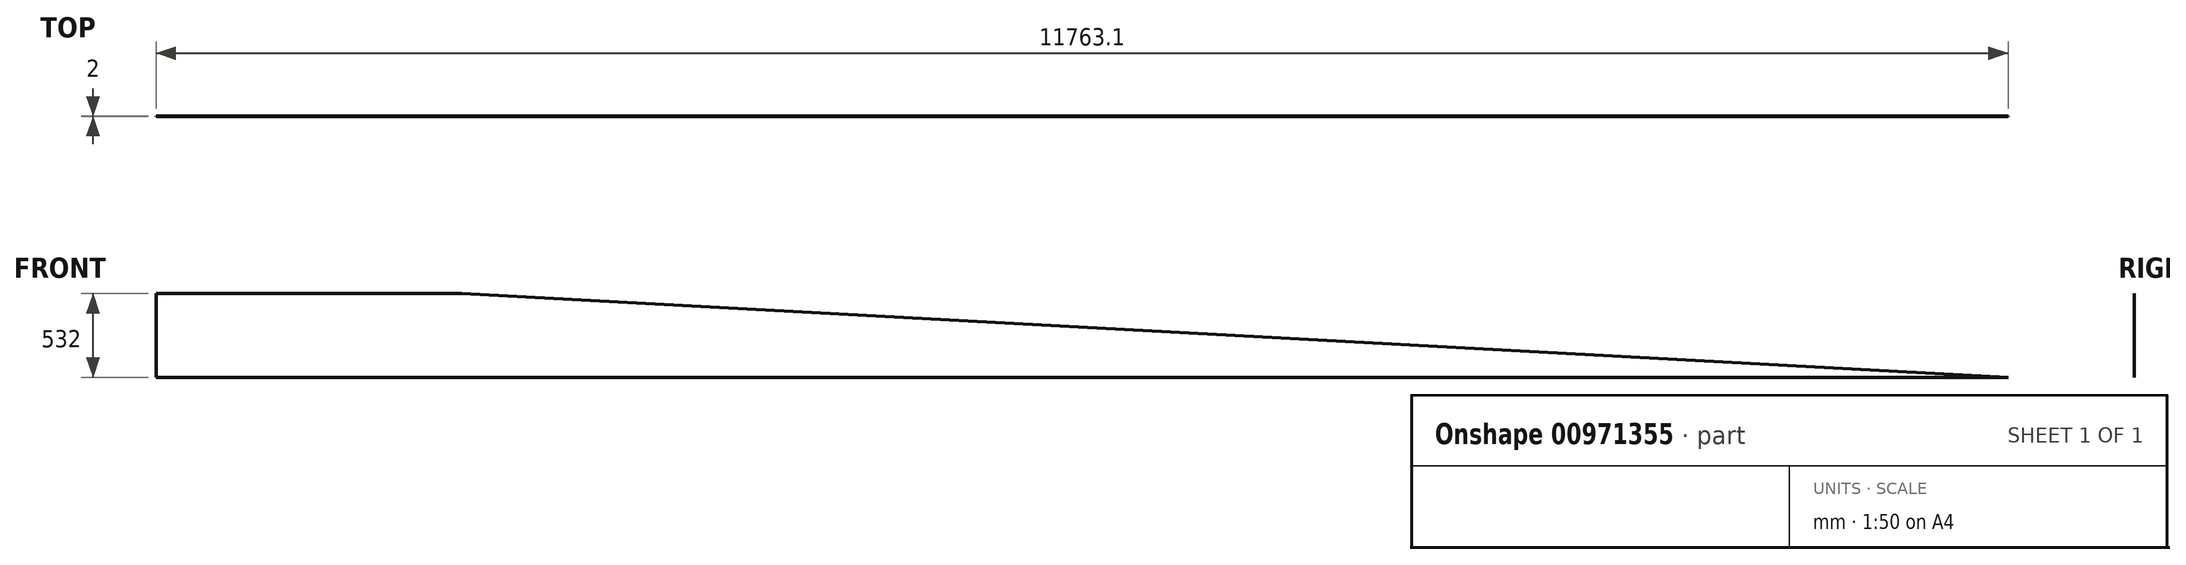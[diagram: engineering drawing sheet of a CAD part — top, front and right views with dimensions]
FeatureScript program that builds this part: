
annotation { "Feature Type Name" : "Feature", "Feature Type Description" : "" }
export const myFeature = defineFeature(function(context is Context, id is Id, definition is map)
    precondition{}
    {
        {
            var Q0;
            Q0=qCreatedBy(makeId("Front.planeOp"),FACE);
            var sketch = newSketch(context, id + "F0", { "sketchPlane" : qUnion([Q0])});
            skLineSegment(sketch, "E0", {"start": v(0, 0) * mm, "end": v(0, 532) * mm});
            skLineSegment(sketch, "E1", {"start": v(0, 532) * mm, "end": v(1940, 532) * mm});
            skLineSegment(sketch, "E2", {"start": v(0, 0) * mm, "end": v(11763.1, 0) * mm});
            skLineSegment(sketch, "E3", {"start": v(1940, 532) * mm, "end": v(11763.1, 0) * mm});
            skSolve(sketch);
        }
        {
            var Q0;
            Q0=makeQuery(id+"F0.imprint","IMPRINT",FACE,{"disambiguationData":[TD([[makeQuery(id+"F0.imprint","IMPRINT",EDGE,{"derivedFrom":sQuery(id+"F0.wireOp",EDGE,"E0")}),-1.0]])]});
            extrude(context, id + "F1", {"entities" : qUnion([Q0]), "depth" : 2 * mm, "offsetDistance" : 25 * mm});
        }
    });
